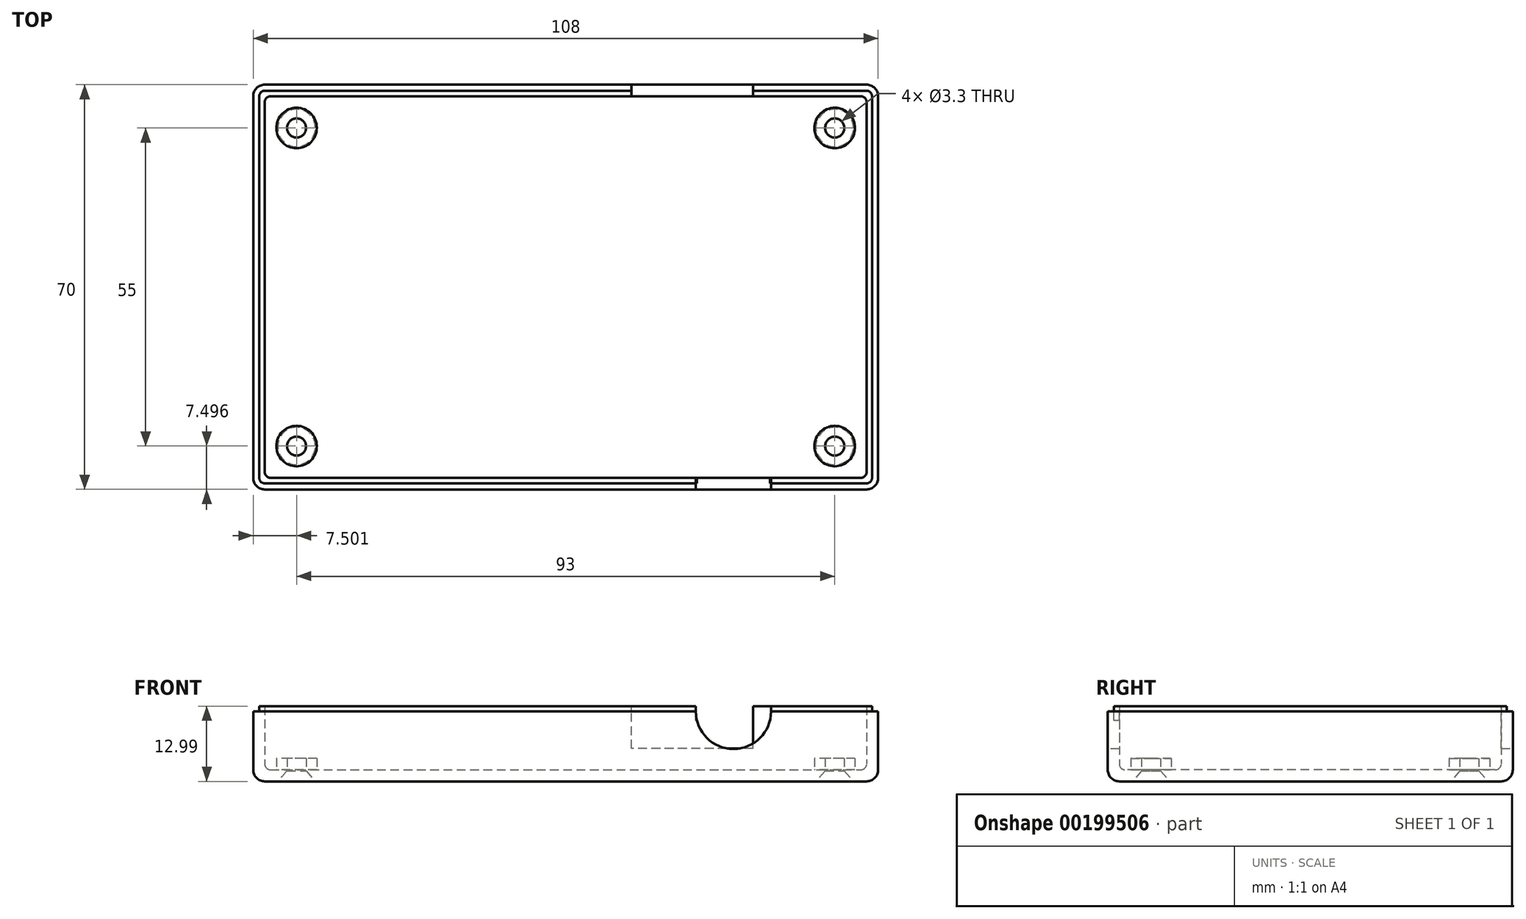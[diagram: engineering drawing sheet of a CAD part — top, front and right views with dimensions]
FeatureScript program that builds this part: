
annotation { "Feature Type Name" : "Feature", "Feature Type Description" : "" }
export const myFeature = defineFeature(function(context is Context, id is Id, definition is map)
    precondition{}
    {
        {
            var Q0;
            Q0=qCreatedBy(makeId("Top.planeOp"),FACE);
            var sketch = newSketch(context, id + "F0", { "sketchPlane" : qUnion([Q0])});
            skLineSegment(sketch, "E0.bottom", {"start": v(-42.36, 21.88) * mm, "end": v(61.64, 21.88) * mm});
            skLineSegment(sketch, "E0.top", {"start": v(-42.36, -48.12) * mm, "end": v(61.64, -48.12) * mm});
            skLineSegment(sketch, "E0.left", {"start": v(-44.36, 19.88) * mm, "end": v(-44.36, -46.12) * mm});
            skLineSegment(sketch, "E0.right", {"start": v(63.64, 19.88) * mm, "end": v(63.64, -46.12) * mm});
            skLineSegment(sketch, "E1.bottom", {"start": v(-42.36, 20.83) * mm, "end": v(61.64, 20.83) * mm});
            skLineSegment(sketch, "E1.top", {"start": v(-42.36, -47.07) * mm, "end": v(61.64, -47.07) * mm});
            skLineSegment(sketch, "E1.left", {"start": v(-43.3, 19.88) * mm, "end": v(-43.3, -46.12) * mm});
            skLineSegment(sketch, "E1.right", {"start": v(62.6, 19.88) * mm, "end": v(62.6, -46.12) * mm});
            skLineSegment(sketch, "E2.bottom", {"start": v(-42.36, 19.88) * mm, "end": v(61.64, 19.88) * mm});
            skLineSegment(sketch, "E2.top", {"start": v(-42.36, -46.12) * mm, "end": v(61.64, -46.12) * mm});
            skLineSegment(sketch, "E2.left", {"start": v(-42.36, 19.88) * mm, "end": v(-42.36, -46.12) * mm});
            skLineSegment(sketch, "E2.right", {"start": v(61.64, 19.88) * mm, "end": v(61.64, -46.12) * mm});
            skCircle(sketch, "E3", {"center": v(-36.86, 14.38) * mm, "radius": 3 * mm});
            skCircle(sketch, "E4", {"center": v(57.14, 14.38) * mm, "radius": 3 * mm});
            skCircle(sketch, "E5", {"center": v(57.14, -40.62) * mm, "radius": 3 * mm});
            skCircle(sketch, "E6", {"center": v(-36.86, -40.62) * mm, "radius": 3 * mm});
            skPoint(sketch, "E7.visualSharp", {"position": v(-44.36, 21.88) * mm});
            skArc(sketch, "E7.filletArc", {"start": v(-42.36, 21.88) * mm, "mid": v(-43.77, 21.3) * mm, "end": v(-44.36, 19.88) * mm});
            skPoint(sketch, "E8.visualSharp", {"position": v(63.64, 21.88) * mm});
            skArc(sketch, "E8.filletArc", {"start": v(63.64, 19.88) * mm, "mid": v(63.06, 21.3) * mm, "end": v(61.64, 21.88) * mm});
            skPoint(sketch, "E9.visualSharp", {"position": v(63.64, -48.12) * mm});
            skArc(sketch, "E9.filletArc", {"start": v(61.64, -48.12) * mm, "mid": v(63.06, -47.54) * mm, "end": v(63.64, -46.12) * mm});
            skPoint(sketch, "E10.visualSharp", {"position": v(-44.36, -48.12) * mm});
            skArc(sketch, "E10.filletArc", {"start": v(-44.36, -46.12) * mm, "mid": v(-43.77, -47.54) * mm, "end": v(-42.36, -48.12) * mm});
            skPoint(sketch, "E11.visualSharp", {"position": v(-43.3, 20.83) * mm});
            skArc(sketch, "E11.filletArc", {"start": v(-42.36, 20.83) * mm, "mid": v(-43.03, 20.55) * mm, "end": v(-43.3, 19.88) * mm});
            skPoint(sketch, "E12.visualSharp", {"position": v(62.6, 20.83) * mm});
            skArc(sketch, "E12.filletArc", {"start": v(62.6, 19.88) * mm, "mid": v(62.31, 20.55) * mm, "end": v(61.64, 20.83) * mm});
            skPoint(sketch, "E13.visualSharp", {"position": v(62.6, -47.07) * mm});
            skArc(sketch, "E13.filletArc", {"start": v(61.64, -47.07) * mm, "mid": v(62.31, -46.8) * mm, "end": v(62.6, -46.12) * mm});
            skPoint(sketch, "E14.visualSharp", {"position": v(-43.3, -47.07) * mm});
            skArc(sketch, "E14.filletArc", {"start": v(-43.3, -46.12) * mm, "mid": v(-43.03, -46.8) * mm, "end": v(-42.36, -47.07) * mm});
            skSolve(sketch);
        }
        {
            var Q0;
            Q0=makeQuery(id+"F0.imprint","IMPRINT",FACE,{"disambiguationData":[TD([[makeQuery(id+"F0.imprint","IMPRINT",EDGE,{"derivedFrom":sQuery(id+"F0.wireOp",EDGE,"E2.bottom")}),-1.0]])]});
            var Q1;
            Q1=makeQuery(id+"F0.imprint","IMPRINT",FACE,{"disambiguationData":[TD([[makeQuery(id+"F0.imprint","IMPRINT",EDGE,{"derivedFrom":sQuery(id+"F0.wireOp",EDGE,"E1.bottom")}),-1.0]])]});
            var Q2;
            Q2=makeQuery(id+"F0.imprint","IMPRINT",FACE,{"disambiguationData":[TD([[makeQuery(id+"F0.imprint","IMPRINT",EDGE,{"derivedFrom":sQuery(id+"F0.wireOp",EDGE,"E0.bottom")}),-1.0]])]});
            var Q3;
            Q3=makeQuery(id+"F0.imprint","IMPRINT",FACE,{"disambiguationData":[TD([[makeQuery(id+"F0.imprint","IMPRINT",EDGE,{"derivedFrom":sQuery(id+"F0.wireOp",EDGE,"E6")}),1.0]])]});
            var Q4;
            Q4=makeQuery(id+"F0.imprint","IMPRINT",FACE,{"disambiguationData":[TD([[makeQuery(id+"F0.imprint","IMPRINT",EDGE,{"derivedFrom":sQuery(id+"F0.wireOp",EDGE,"E5")}),1.0]])]});
            var Q5;
            Q5=makeQuery(id+"F0.imprint","IMPRINT",FACE,{"disambiguationData":[TD([[makeQuery(id+"F0.imprint","IMPRINT",EDGE,{"derivedFrom":sQuery(id+"F0.wireOp",EDGE,"E3")}),1.0]])]});
            var Q6;
            Q6=makeQuery(id+"F0.imprint","IMPRINT",FACE,{"disambiguationData":[TD([[makeQuery(id+"F0.imprint","IMPRINT",EDGE,{"derivedFrom":sQuery(id+"F0.wireOp",EDGE,"E4")}),1.0]])]});
            extrude(context, id + "F1", {"entities" : qUnion([Q0, Q1, Q2, Q3, Q4, Q5, Q6]), "oppositeDirection" : true, "depth" : 2 * mm});
        }
        {
            var Q0;
            Q0=makeQuery(id+"F0.imprint","IMPRINT",FACE,{"disambiguationData":[TD([[makeQuery(id+"F0.imprint","IMPRINT",EDGE,{"derivedFrom":sQuery(id+"F0.wireOp",EDGE,"E1.bottom")}),-1.0]])]});
            extrude(context, id + "F2", {"entities" : qUnion([Q0]), "operationType" : NewBodyOperationType.ADD, "depth" : 11 * mm});
        }
        {
            var Q0;
            Q0=qSketchRegion(id+"F0",true);
            extrude(context, id + "F3", {"entities" : qUnion([Q0]), "operationType" : NewBodyOperationType.ADD, "depth" : 10.1 * mm});
        }
        {
            var Q0;
            Q0=makeQuery(id+"F2.boolean.opBoolean","SPLIT",FACE,{"disambiguationData":[TD([makeQuery(id+"F2.opExtrude","SWEPT_FACE",FACE,{"disambiguationData":[OSD([sQuery(id+"F0.wireOp",EDGE,"E2.bottom")])]})])],"derivedFrom":makeQuery(id+"F1.opExtrude","CAP_FACE",FACE,{"disambiguationData":[OSD([sQuery(id+"F0.wireOp",EDGE,"E0.bottom"),sQuery(id+"F0.wireOp",EDGE,"E0.top"),sQuery(id+"F0.wireOp",EDGE,"E0.left"),sQuery(id+"F0.wireOp",EDGE,"E0.right")])],"isStart":true})});
            var sketch = newSketch(context, id + "F4", { "sketchPlane" : qUnion([Q0])});
            skCircle(sketch, "E15", {"center": v(-36.86, 14.38) * mm, "radius": 3.5 * mm});
            skCircle(sketch, "E16", {"center": v(56.14, 14.38) * mm, "radius": 3.5 * mm});
            skCircle(sketch, "E17", {"center": v(-36.86, -40.62) * mm, "radius": 3.5 * mm});
            skCircle(sketch, "E18", {"center": v(56.14, -40.62) * mm, "radius": 3.5 * mm});
            skSolve(sketch);
        }
        {
            var Q0;
            Q0=makeQuery(id+"F4.imprint","IMPRINT",FACE,{"disambiguationData":[TD([[makeQuery(id+"F4.imprint","IMPRINT",EDGE,{"derivedFrom":sQuery(id+"F4.wireOp",EDGE,"E15")}),1.0]])]});
            var Q1;
            Q1=makeQuery(id+"F4.imprint","IMPRINT",FACE,{"disambiguationData":[TD([[makeQuery(id+"F4.imprint","IMPRINT",EDGE,{"derivedFrom":sQuery(id+"F4.wireOp",EDGE,"E16")}),1.0]])]});
            var Q2;
            Q2=makeQuery(id+"F4.imprint","IMPRINT",FACE,{"disambiguationData":[TD([[makeQuery(id+"F4.imprint","IMPRINT",EDGE,{"derivedFrom":sQuery(id+"F4.wireOp",EDGE,"E18")}),1.0]])]});
            var Q3;
            Q3=makeQuery(id+"F4.imprint","IMPRINT",FACE,{"disambiguationData":[TD([[makeQuery(id+"F4.imprint","IMPRINT",EDGE,{"derivedFrom":sQuery(id+"F4.wireOp",EDGE,"E17")}),1.0]])]});
            extrude(context, id + "F5", {"entities" : qUnion([Q0, Q1, Q2, Q3]), "operationType" : NewBodyOperationType.ADD, "depth" : 2 * mm});
        }
        {
            var Q0;
            Q0=makeQuery(id+"F1.opExtrude","CAP_FACE",FACE,{"disambiguationData":[OSD([sQuery(id+"F0.wireOp",EDGE,"E0.bottom"),sQuery(id+"F0.wireOp",EDGE,"E0.top"),sQuery(id+"F0.wireOp",EDGE,"E0.left"),sQuery(id+"F0.wireOp",EDGE,"E0.right")])],"isStart":false});
            var sketch = newSketch(context, id + "F6", { "sketchPlane" : qUnion([Q0])});
            skPoint(sketch, "E19", {"position": v(-36.86, 40.62) * mm});
            skPoint(sketch, "E20", {"position": v(-36.86, -14.38) * mm});
            skPoint(sketch, "E21", {"position": v(56.14, 40.62) * mm});
            skPoint(sketch, "E22", {"position": v(56.14, -14.38) * mm});
            skSolve(sketch);
        }
        {
            var Q0;
            Q0=sQuery(id+"F6.wireOp",VERTEX,"E19");
            var Q1;
            Q1=sQuery(id+"F6.wireOp",VERTEX,"E21");
            var Q2;
            Q2=sQuery(id+"F6.wireOp",VERTEX,"E22");
            var Q3;
            Q3=sQuery(id+"F6.wireOp",VERTEX,"E20");
            var Q4;
            Q4=makeQuery(id+"F1.opExtrude","SWEPT_BODY",BODY,{"disambiguationData":[OSD([sQuery(id+"F0.wireOp",EDGE,"E0.bottom"),sQuery(id+"F0.wireOp",EDGE,"E0.top"),sQuery(id+"F0.wireOp",EDGE,"E0.left"),sQuery(id+"F0.wireOp",EDGE,"E0.right")])]});
            hole(context, id + "F7", {"style" : HoleStyle.C_SINK, "endStyle" : HoleEndStyle.THROUGH, "holeDiameter" : 3.3 * mm, "cSinkDiameter" : 6.48 * mm, "cSinkAngle" : 82 * degree, "startFromSketch" : true, "locations" : qUnion([Q0, Q1, Q2, Q3]), "scope" : qUnion([Q4]), "tappedDepth" : 12 * mm, "tapClearance" : 3});
        }
        {
            var Q0;
            {var subQ0=sQuery(id+"F0.wireOp",EDGE,"E0.bottom");Q0=makeQuery(id+"F3.boolean.opBoolean","MERGE",FACE,{"derivedFrom":[makeQuery(id+"F1.opExtrude","SWEPT_FACE",FACE,{"disambiguationData":[OSD([subQ0])]}),makeQuery(id+"F3.opExtrude","SWEPT_FACE",FACE,{"disambiguationData":[OSD([subQ0])]})]});}
            var sketch = newSketch(context, id + "F8", { "sketchPlane" : qUnion([Q0])});
            skLineSegment(sketch, "E23.bottom", {"start": v(-42.04, 3.7) * mm, "end": v(-21.04, 3.7) * mm});
            skLineSegment(sketch, "E23.top", {"start": v(-42.04, 10.1) * mm, "end": v(-21.04, 10.1) * mm});
            skLineSegment(sketch, "E23.left", {"start": v(-42.04, 3.7) * mm, "end": v(-42.04, 10.1) * mm});
            skLineSegment(sketch, "E23.right", {"start": v(-21.04, 3.7) * mm, "end": v(-21.04, 10.1) * mm});
            skSolve(sketch);
        }
        {
            var Q0;
            Q0=makeQuery(id+"F8.imprint","IMPRINT",FACE,{"disambiguationData":[TD([[makeQuery(id+"F8.imprint","IMPRINT",EDGE,{"derivedFrom":sQuery(id+"F8.wireOp",EDGE,"E23.bottom")}),1.0]])]});
            extrude(context, id + "F9", {"entities" : qUnion([Q0]), "operationType" : NewBodyOperationType.REMOVE, "oppositeDirection" : true, "depth" : 2.5 * mm});
        }
        {
            var Q0;
            Q0=makeQuery(id+"F2.opExtrude","CAP_FACE",FACE,{"disambiguationData":[OSD([sQuery(id+"F0.wireOp",EDGE,"E1.bottom"),sQuery(id+"F0.wireOp",EDGE,"E1.top"),sQuery(id+"F0.wireOp",EDGE,"E1.left"),sQuery(id+"F0.wireOp",EDGE,"E1.right"),sQuery(id+"F0.wireOp",EDGE,"E2.bottom"),sQuery(id+"F0.wireOp",EDGE,"E2.top"),sQuery(id+"F0.wireOp",EDGE,"E2.left"),sQuery(id+"F0.wireOp",EDGE,"E2.right")])],"isStart":false});
            var sketch = newSketch(context, id + "F10", { "sketchPlane" : qUnion([Q0])});
            skLineSegment(sketch, "E24.bottom", {"start": v(32.14, -44.62) * mm, "end": v(45.14, -44.62) * mm});
            skLineSegment(sketch, "E24.top", {"start": v(32.14, -47.62) * mm, "end": v(45.14, -47.62) * mm});
            skLineSegment(sketch, "E24.left", {"start": v(32.14, -44.62) * mm, "end": v(32.14, -47.62) * mm});
            skLineSegment(sketch, "E24.right", {"start": v(45.14, -44.62) * mm, "end": v(45.14, -47.62) * mm});
            skLineSegment(sketch, "E25.bottom", {"start": v(21.04, 22.83) * mm, "end": v(42.04, 22.83) * mm});
            skLineSegment(sketch, "E25.top", {"start": v(21.04, 17.83) * mm, "end": v(42.04, 17.83) * mm});
            skLineSegment(sketch, "E25.left", {"start": v(21.04, 22.83) * mm, "end": v(21.04, 17.83) * mm});
            skLineSegment(sketch, "E25.right", {"start": v(42.04, 22.83) * mm, "end": v(42.04, 17.83) * mm});
            skSolve(sketch);
        }
        {
            var Q0;
            {var subQ0=sQuery(id+"F10.wireOp",EDGE,"GH5rCHhh-geM3-sB2K-jFEz-GMiepMDtVWYR.bottom");Q0=makeQuery(id+"F10.imprint","IMPRINT",FACE,{"disambiguationData":[TD([[makeQuery(id+"F10.imprint","IMPRINT",EDGE,{"derivedFrom":subQ0}),-1.0]])]});}
            var Q1;
            {var subQ0=sQuery(id+"F10.wireOp",EDGE,"E24.left");var subQ1=makeQuery(id+"F2.opExtrude","CAP_EDGE",EDGE,{"disambiguationData":[OSD([sQuery(id+"F0.wireOp",EDGE,"E1.top")])],"isStart":false});var subQ2=makeQuery(id+"F10.imprint","INTERSECT",VERTEX,{"derivedFrom":[subQ1,subQ0]});Q1=makeQuery(id+"F10.imprint","IMPRINT",FACE,{"disambiguationData":[TD([[makeQuery(id+"F10.imprint","IMPRINT",EDGE,{"disambiguationData":[TD([[subQ2,1.0]])],"derivedFrom":subQ0}),1.0]])]});}
            extrude(context, id + "F11", {"entities" : qUnion([Q0, Q1]), "operationType" : NewBodyOperationType.REMOVE, "oppositeDirection" : true, "depth" : 2.5 * mm});
        }
        {
            var Q0;
            {var subQ0=sQuery(id+"F0.wireOp",EDGE,"E0.top");Q0=makeQuery(id+"F3.boolean.opBoolean","MERGE",FACE,{"derivedFrom":[makeQuery(id+"F1.opExtrude","SWEPT_FACE",FACE,{"disambiguationData":[OSD([subQ0])]}),makeQuery(id+"F3.opExtrude","SWEPT_FACE",FACE,{"disambiguationData":[OSD([subQ0])]})]});}
            var sketch = newSketch(context, id + "F12", { "sketchPlane" : qUnion([Q0])});
            skPoint(sketch, "E26", {"position": v(38.64, 10.1) * mm});
            skCircle(sketch, "E27", {"center": v(38.64, 10.1) * mm, "radius": 6.5 * mm});
            skSolve(sketch);
        }
        {
            var Q0;
            {var subQ0=sQuery(id+"F12.wireOp",EDGE,"E27");var subQ1=makeQuery(id+"F3.opExtrude","CAP_EDGE",EDGE,{"disambiguationData":[OSD([sQuery(id+"F0.wireOp",EDGE,"E0.top")])],"isStart":false});var subQ2=makeQuery(id+"F12.imprint","INTERSECT",VERTEX,{"disambiguationData":[OD(0.0)],"derivedFrom":[subQ1,subQ0]});Q0=makeQuery(id+"F12.imprint","IMPRINT",FACE,{"disambiguationData":[TD([[makeQuery(id+"F12.imprint","IMPRINT",EDGE,{"disambiguationData":[TD([[subQ2,-1.0]])],"derivedFrom":subQ0}),1.0]])]});}
            extrude(context, id + "F13", {"entities" : qUnion([Q0]), "operationType" : NewBodyOperationType.REMOVE, "oppositeDirection" : true, "depth" : 2.5 * mm});
        }
        {
            var Q0;
            {var subQ0=sQuery(id+"F0.wireOp",EDGE,"E0.right");var subQ1=sQuery(id+"F0.wireOp",EDGE,"E0.top");Q0=makeQuery(id+"F3.boolean.opBoolean","MERGE",EDGE,{"derivedFrom":[makeQuery(id+"F1.opExtrude","SWEPT_EDGE",EDGE,{"disambiguationData":[OSD([subQ1,subQ0])]}),makeQuery(id+"F3.opExtrude","SWEPT_EDGE",EDGE,{"disambiguationData":[OSD([subQ1,subQ0])]})]});}
            var Q1;
            Q1=makeQuery(id+"F1.opExtrude","CAP_EDGE",EDGE,{"disambiguationData":[OSD([sQuery(id+"F0.wireOp",EDGE,"E0.right")])],"isStart":false});
            var Q2;
            {var subQ0=sQuery(id+"F0.wireOp",EDGE,"E0.right");var subQ1=sQuery(id+"F0.wireOp",EDGE,"E0.bottom");Q2=makeQuery(id+"F3.boolean.opBoolean","MERGE",EDGE,{"derivedFrom":[makeQuery(id+"F1.opExtrude","SWEPT_EDGE",EDGE,{"disambiguationData":[OSD([subQ1,subQ0])]}),makeQuery(id+"F3.opExtrude","SWEPT_EDGE",EDGE,{"disambiguationData":[OSD([subQ1,subQ0])]})]});}
            var Q3;
            Q3=makeQuery(id+"F1.opExtrude","CAP_EDGE",EDGE,{"disambiguationData":[OSD([sQuery(id+"F0.wireOp",EDGE,"E0.bottom")])],"isStart":false});
            var Q4;
            {var subQ0=sQuery(id+"F0.wireOp",EDGE,"E0.left");var subQ1=sQuery(id+"F0.wireOp",EDGE,"E0.bottom");Q4=makeQuery(id+"F3.boolean.opBoolean","MERGE",EDGE,{"derivedFrom":[makeQuery(id+"F1.opExtrude","SWEPT_EDGE",EDGE,{"disambiguationData":[OSD([subQ1,subQ0])]}),makeQuery(id+"F3.opExtrude","SWEPT_EDGE",EDGE,{"disambiguationData":[OSD([subQ1,subQ0])]})]});}
            var Q5;
            {var subQ0=sQuery(id+"F0.wireOp",EDGE,"E0.left");var subQ1=sQuery(id+"F0.wireOp",EDGE,"E0.top");Q5=makeQuery(id+"F3.boolean.opBoolean","MERGE",EDGE,{"derivedFrom":[makeQuery(id+"F1.opExtrude","SWEPT_EDGE",EDGE,{"disambiguationData":[OSD([subQ1,subQ0])]}),makeQuery(id+"F3.opExtrude","SWEPT_EDGE",EDGE,{"disambiguationData":[OSD([subQ1,subQ0])]})]});}
            var Q6;
            Q6=makeQuery(id+"F1.opExtrude","CAP_EDGE",EDGE,{"disambiguationData":[OSD([sQuery(id+"F0.wireOp",EDGE,"E0.left")])],"isStart":false});
            var Q7;
            Q7=makeQuery(id+"F1.opExtrude","CAP_EDGE",EDGE,{"disambiguationData":[OSD([sQuery(id+"F0.wireOp",EDGE,"E0.top")])],"isStart":false});
            fillet(context, id + "F14", {"entities" : qUnion([Q0, Q1, Q2, Q3, Q4, Q5, Q6, Q7]), "radius" : 2 * mm, "tangentPropagation" : true, "allowEdgeOverflow" : false});
        }
        {
            var Q0;
            Q0=makeQuery(id+"F2.opExtrude","CAP_EDGE",EDGE,{"disambiguationData":[OSD([sQuery(id+"F0.wireOp",EDGE,"E2.bottom")])],"isStart":true});
            var Q1;
            Q1=makeQuery(id+"F2.opExtrude","SWEPT_EDGE",EDGE,{"disambiguationData":[OSD([sQuery(id+"F0.wireOp",EDGE,"E2.bottom"),sQuery(id+"F0.wireOp",EDGE,"E2.left")])]});
            var Q2;
            Q2=makeQuery(id+"F2.opExtrude","CAP_EDGE",EDGE,{"disambiguationData":[OSD([sQuery(id+"F0.wireOp",EDGE,"E2.left")])],"isStart":true});
            var Q3;
            Q3=makeQuery(id+"F2.opExtrude","CAP_EDGE",EDGE,{"disambiguationData":[OSD([sQuery(id+"F0.wireOp",EDGE,"E2.top")])],"isStart":true});
            var Q4;
            Q4=makeQuery(id+"F2.opExtrude","SWEPT_EDGE",EDGE,{"disambiguationData":[OSD([sQuery(id+"F0.wireOp",EDGE,"E2.top"),sQuery(id+"F0.wireOp",EDGE,"E2.left")])]});
            var Q5;
            Q5=makeQuery(id+"F2.opExtrude","SWEPT_EDGE",EDGE,{"disambiguationData":[OSD([sQuery(id+"F0.wireOp",EDGE,"E2.bottom"),sQuery(id+"F0.wireOp",EDGE,"E2.right")])]});
            var Q6;
            Q6=makeQuery(id+"F2.opExtrude","CAP_EDGE",EDGE,{"disambiguationData":[OSD([sQuery(id+"F0.wireOp",EDGE,"E2.right")])],"isStart":true});
            var Q7;
            Q7=makeQuery(id+"F2.opExtrude","SWEPT_EDGE",EDGE,{"disambiguationData":[OSD([sQuery(id+"F0.wireOp",EDGE,"E2.top"),sQuery(id+"F0.wireOp",EDGE,"E2.right")])]});
            fillet(context, id + "F15", {"entities" : qUnion([Q0, Q1, Q2, Q3, Q4, Q5, Q6, Q7]), "radius" : 1 * mm, "tangentPropagation" : true, "allowEdgeOverflow" : false});
        }
        {
            var Q0;
            Q0=makeQuery(id+"F2.opExtrude","SWEPT_FACE",FACE,{"disambiguationData":[OSD([sQuery(id+"F0.wireOp",EDGE,"E1.bottom")])]});
            var sketch = newSketch(context, id + "F16", { "sketchPlane" : qUnion([Q0])});
            skLineSegment(sketch, "E28.bottom", {"start": v(-21.04, 10.1) * mm, "end": v(-42.04, 10.1) * mm});
            skLineSegment(sketch, "E28.top", {"start": v(-21.04, 11) * mm, "end": v(-42.04, 11) * mm});
            skLineSegment(sketch, "E28.left", {"start": v(-21.04, 10.1) * mm, "end": v(-21.04, 11) * mm});
            skLineSegment(sketch, "E28.right", {"start": v(-42.04, 10.1) * mm, "end": v(-42.04, 11) * mm});
            skSolve(sketch);
        }
        {
            var Q0;
            Q0=makeQuery(id+"F16.imprint","IMPRINT",FACE,{"disambiguationData":[TD([[makeQuery(id+"F16.imprint","IMPRINT",EDGE,{"derivedFrom":sQuery(id+"F16.wireOp",EDGE,"E28.bottom")}),-1.0]])]});
            extrude(context, id + "F17", {"entities" : qUnion([Q0]), "operationType" : NewBodyOperationType.REMOVE, "oppositeDirection" : true, "depth" : 2.5 * mm});
        }
    });
